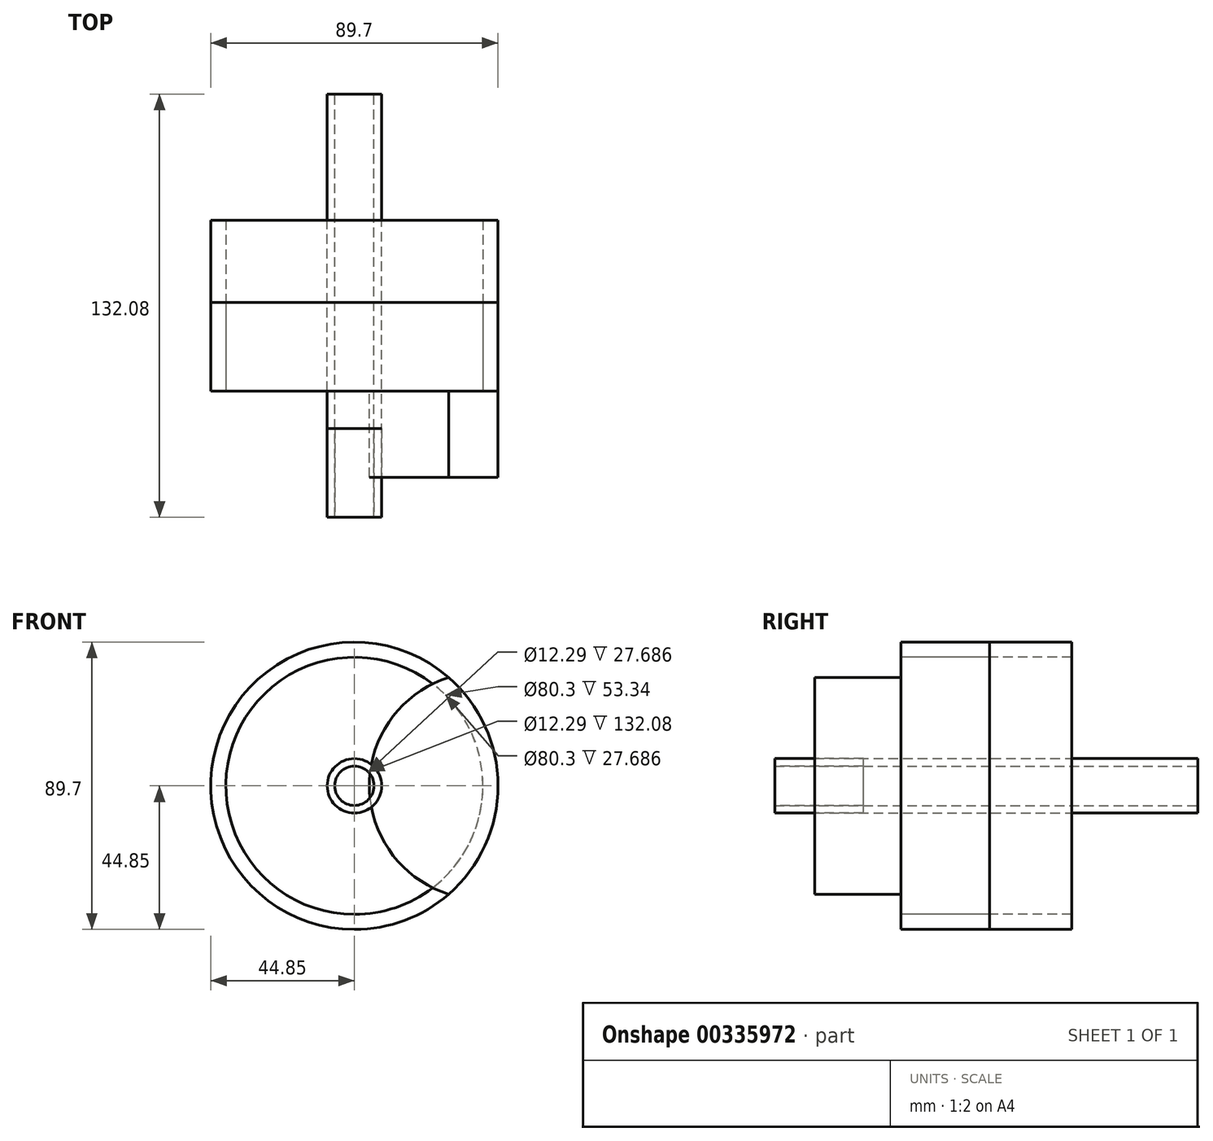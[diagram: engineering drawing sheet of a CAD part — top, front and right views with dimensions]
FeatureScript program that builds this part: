
annotation { "Feature Type Name" : "Feature", "Feature Type Description" : "" }
export const myFeature = defineFeature(function(context is Context, id is Id, definition is map)
    precondition{}
    {
        {
            var Q0;
            Q0=qCreatedBy(makeId("Front.planeOp"),FACE);
            var sketch = newSketch(context, id + "F0", { "sketchPlane" : qUnion([Q0])});
            skCircle(sketch, "E0", {"center": v(0, 0) * mm, "radius": 40.15 * mm});
            skCircle(sketch, "E1", {"center": v(0, 0) * mm, "radius": 6.3 * mm});
            skCircle(sketch, "E2", {"center": v(0, 0) * mm, "radius": 44.85 * mm});
            skSolve(sketch);
        }
        {
            var Q0;
            Q0=qCreatedBy(makeId("Front.planeOp"),FACE);
            var sketch = newSketch(context, id + "F1", { "sketchPlane" : qUnion([Q0])});
            skCircle(sketch, "E3", {"center": v(0, 0) * mm, "radius": 6.14 * mm});
            skCircle(sketch, "E4", {"center": v(0, 0) * mm, "radius": 30.68 * mm});
            skCircle(sketch, "E5", {"center": v(0, 0) * mm, "radius": 34.8 * mm});
            skCircle(sketch, "E6", {"center": v(0, 0) * mm, "radius": 8.5 * mm});
            skSolve(sketch);
        }
        {
            var Q0;
            Q0=makeQuery(id+"F1.imprint","IMPRINT",FACE,{"disambiguationData":[TD([[makeQuery(id+"F1.imprint","IMPRINT",EDGE,{"derivedFrom":sQuery(id+"F1.wireOp",EDGE,"E3")}),-1.0]])]});
            var Q1;
            Q1=sQuery(id+"F1.wireOp",EDGE,"E5");
            var Q2;
            Q2=sQuery(id+"F1.wireOp",EDGE,"E6");
            var Q3;
            Q3=sQuery(id+"F1.wireOp",EDGE,"E3");
            var Q4;
            Q4=sQuery(id+"F1.wireOp",EDGE,"E4");
            extrude(context, id + "F2", {"entities" : qUnion([Q0]), "surfaceEntities" : qUnion([Q1, Q2, Q3, Q4]), "endBound" : BoundingType.SYMMETRIC, "depth" : 132.08 * mm});
        }
        {
            var Q0;
            Q0 = qSketchRegion(id + "F0", true);
            extrude(context, id + "F3", {"entities" : qUnion([Q0]), "operationType" : NewBodyOperationType.ADD, "endBound" : BoundingType.SYMMETRIC, "oppositeDirection" : true, "depth" : 53.34 * mm});
        }
        {
            var Q0;
            Q0=makeQuery(id+"F2.opExtrude","CAP_FACE",FACE,{"disambiguationData":[OSD([sQuery(id+"F1.wireOp",EDGE,"E3"),sQuery(id+"F1.wireOp",EDGE,"E6")])],"isStart":false});
            var Q1;
            Q1=makeQuery(id+"F3.opExtrude","CAP_FACE",FACE,{"disambiguationData":[OSD([sQuery(id+"F0.wireOp",EDGE,"E0"),sQuery(id+"F0.wireOp",EDGE,"E2")])],"isStart":true});
            extrude(context, id + "F4", {"entities" : qUnion([Q0, Q1]), "oppositeDirection" : true, "depth" : 27.7 * mm});
        }
        {
            var Q0;
            Q0=makeQuery(id+"F3.opExtrude","CAP_FACE",FACE,{"disambiguationData":[OSD([sQuery(id+"F0.wireOp",EDGE,"E0"),sQuery(id+"F0.wireOp",EDGE,"E2")])],"isStart":true});
            var sketch = newSketch(context, id + "F5", { "sketchPlane" : qUnion([Q0])});
            skCircle(sketch, "E7", {"center": v(40.15, 0) * mm, "radius": 35.49 * mm});
            skSolve(sketch);
        }
        {
            var Q0;
            {var subQ0=sQuery(id+"F5.wireOp",EDGE,"E7");var subQ1=makeQuery(id+"F3.opExtrude","CAP_EDGE",EDGE,{"disambiguationData":[OSD([sQuery(id+"F0.wireOp",EDGE,"E2")])],"isStart":true});var subQ2=makeQuery(id+"F5.imprint","INTERSECT",VERTEX,{"disambiguationData":[OD(0.0)],"derivedFrom":[subQ1,subQ0]});Q0=makeQuery(id+"F5.imprint","IMPRINT",FACE,{"disambiguationData":[TD([[makeQuery(id+"F5.imprint","IMPRINT",EDGE,{"disambiguationData":[TD([[subQ2,-1.0]])],"derivedFrom":subQ0}),1.0]])]});}
            var Q1;
            {var subQ0=sQuery(id+"F5.wireOp",EDGE,"E7");var subQ1=makeQuery(id+"F3.opExtrude","CAP_EDGE",EDGE,{"disambiguationData":[OSD([sQuery(id+"F0.wireOp",EDGE,"E0")])],"isStart":true});var subQ2=makeQuery(id+"F5.imprint","INTERSECT",VERTEX,{"disambiguationData":[OD(0.0)],"derivedFrom":[subQ1,subQ0]});Q1=makeQuery(id+"F5.imprint","IMPRINT",FACE,{"disambiguationData":[TD([[makeQuery(id+"F5.imprint","IMPRINT",EDGE,{"disambiguationData":[TD([[subQ2,-1.0]])],"derivedFrom":subQ0}),1.0]])]});}
            extrude(context, id + "F6", {"entities" : qUnion([Q0, Q1]), "depth" : 26.92 * mm});
        }
    });
